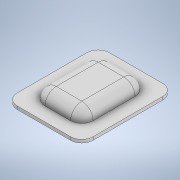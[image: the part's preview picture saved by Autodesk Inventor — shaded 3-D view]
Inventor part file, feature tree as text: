
AUTODESK INVENTOR PART (.ipt)
format: ipt  version: 2020 (Build 240168000, 168)  size: 146,432 bytes
history: native  units: in
note: dims shown in document units (in); Inventor stores cm internally (conversion verified against a paired STEP export)
features: fillet x3, extrude x2, sketch x2
ambient origin geometry x8: Origin, YZ Plane, XZ Plane, XY Plane, X Axis, Y Axis, Z Axis, Center Point
bodies: Solid1 (feature_tree)
feature tree (7):
  extrude  "Extrusion1"  Depth=0.4165in
  fillet  "Fillet1"  Radius=0.4165in
  fillet  "Fillet2"  Radius=0.4165in
  extrude  "Extrusion3"  Depth=0.4165in
  fillet  "Fillet4"  Radius=0.5118in
  sketch  "Sketch1"  dims[d0=1.7795in d1=2.3858in d2=0.4165in d3=0.0in d4=0.4165in]
  sketch  "Sketch3"  dims[d5=0.4165in d14=0.5118in d15=0.5118in d16=0.5118in d17=0.5118in d18=0.1181in d19=0.0in d20=0.4165in d6=0.0344in]
